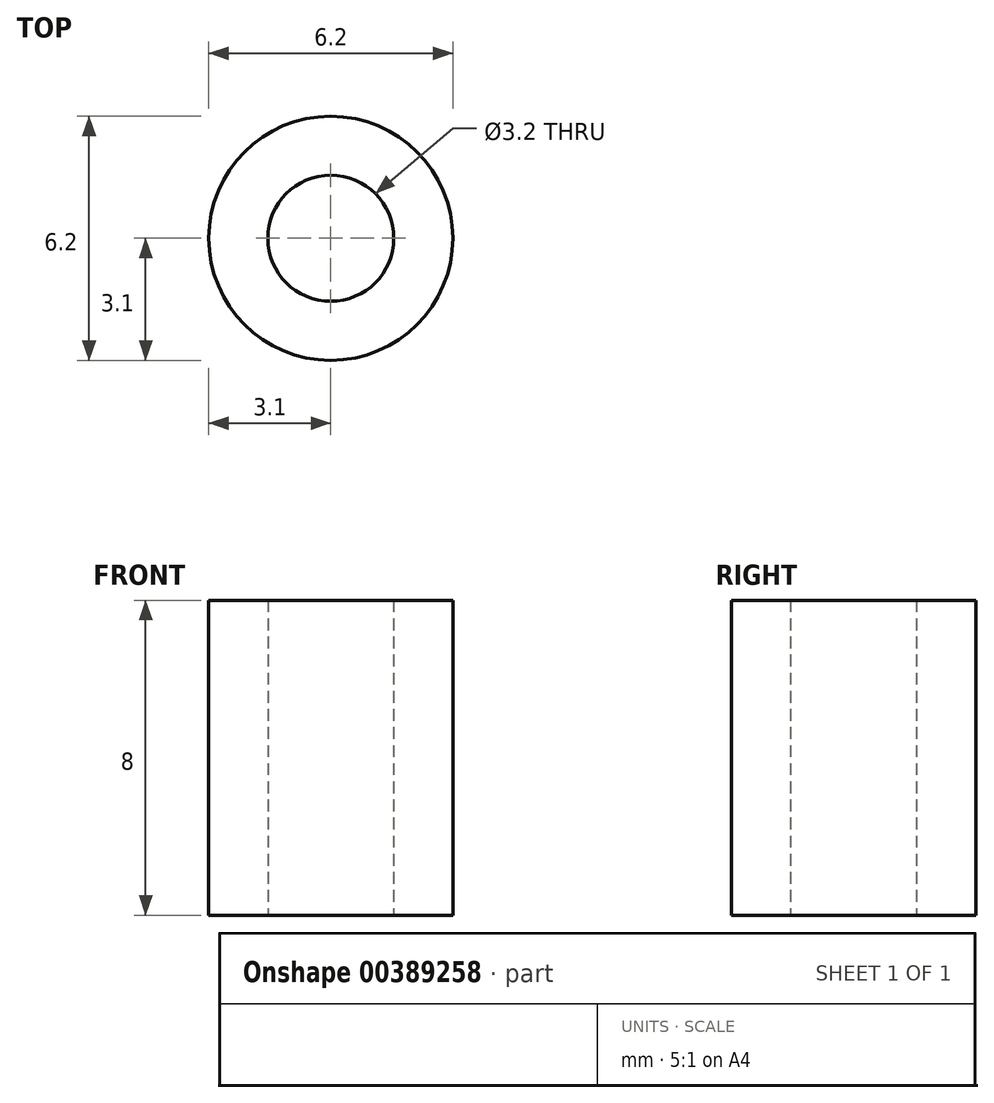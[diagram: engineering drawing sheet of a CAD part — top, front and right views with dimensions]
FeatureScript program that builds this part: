
annotation { "Feature Type Name" : "Feature", "Feature Type Description" : "" }
export const myFeature = defineFeature(function(context is Context, id is Id, definition is map)
    precondition{}
    {
        {
            var Q0;
            Q0=qCreatedBy(makeId("Top.planeOp"), FACE);
            var sketch = newSketch(context, id + "F0", { "sketchPlane" : qUnion([Q0])});
            skCircle(sketch, "E0", {"center": v(0, 0) * mm, "radius": 3.1 * mm});
            skCircle(sketch, "E1", {"center": v(0, 0) * mm, "radius": 1.6 * mm});
            skSolve(sketch);
        }
        {
            var Q0;
            Q0 = qSketchRegion(id + "F0", true);
            extrude(context, id + "F1", {"entities" : qUnion([Q0]), "depth" : 8 * mm, "offsetDistance" : 25 * mm});
        }
    });
